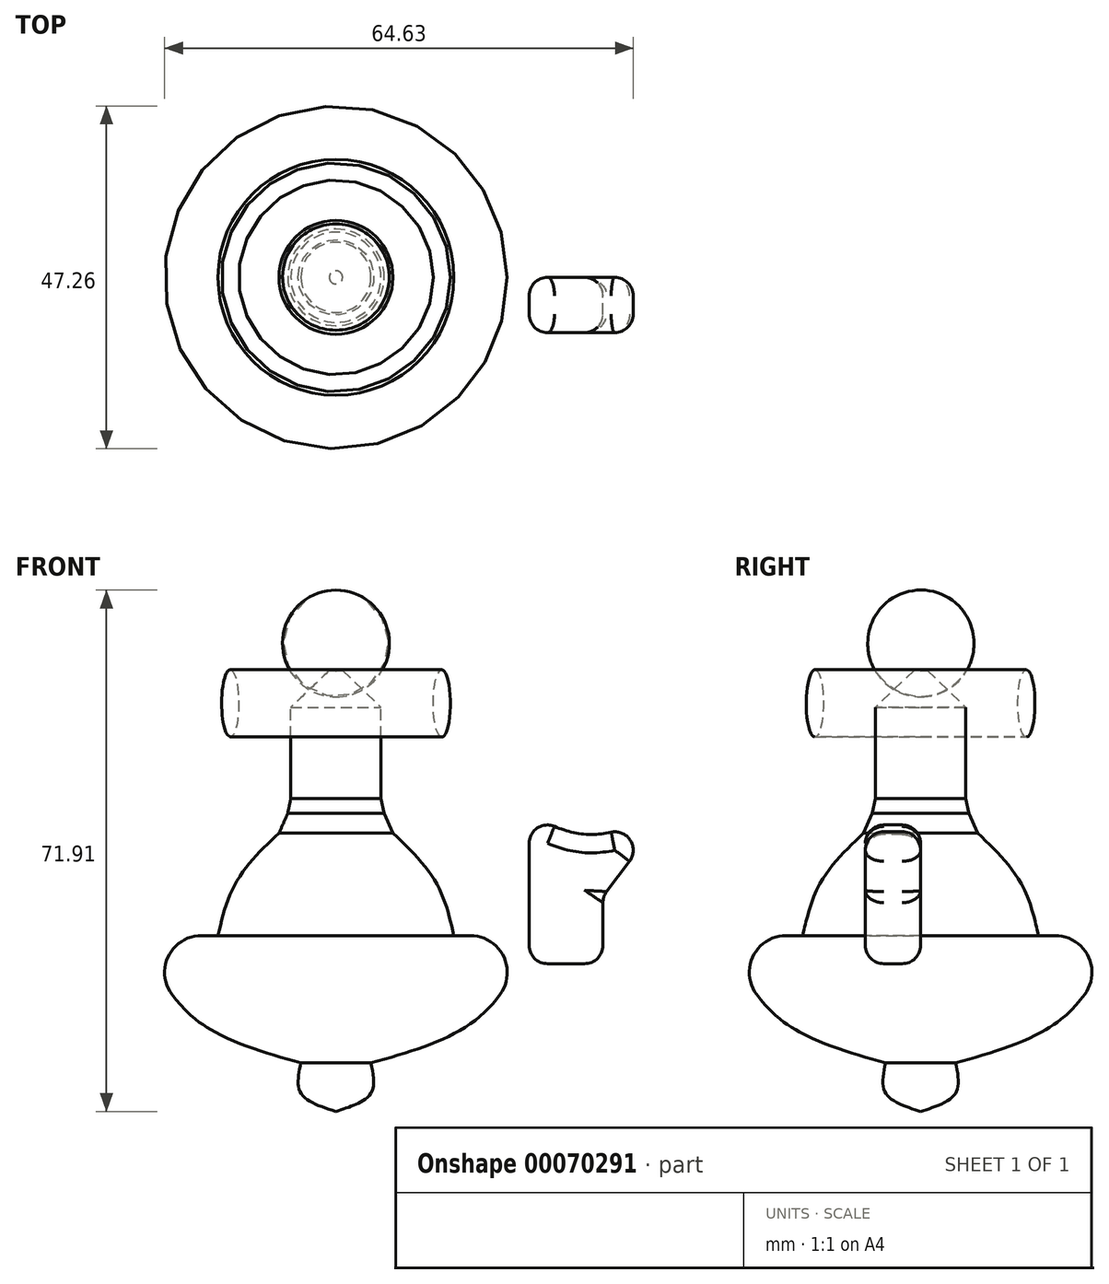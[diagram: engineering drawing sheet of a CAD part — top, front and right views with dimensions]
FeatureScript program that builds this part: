
annotation { "Feature Type Name" : "Feature", "Feature Type Description" : "" }
export const myFeature = defineFeature(function(context is Context, id is Id, definition is map)
    precondition{}
    {
        {
            var Q0;
            Q0=qCreatedBy(makeId("Front.planeOp"),FACE);
            var sketch = newSketch(context, id + "F0", { "sketchPlane" : qUnion([Q0])});
            skLineSegment(sketch, "E0", {"start": v(0, 65.51) * mm, "end": v(0, 4.74) * mm});
            skLineSegment(sketch, "E1", {"start": v(-27.13, 29) * mm, "end": v(-16.26, 29) * mm});
            skLineSegment(sketch, "E2", {"start": v(-6.22, 44.6) * mm, "end": v(-6.22, 65.8) * mm});
            skLineSegment(sketch, "E3", {"start": v(-6.22, 65.8) * mm, "end": v(0, 65.51) * mm});
            skFitSpline(sketch, "E4", {"points": [v(-27.13, 29) * mm, v(-19.63, 17.66) * mm, v(-4.83, 11.43) * mm], "startDerivative": vector(12.61, -26.44) * mm, "endDerivative": vector(31.73, -8.93) * mm});
            skFitSpline(sketch, "E5", {"points": [v(-4.83, 11.43) * mm, v(-4.83, 7.27) * mm, v(0, 4.74) * mm], "startDerivative": vector(-2.1, -9.9) * mm, "endDerivative": vector(11.46, -3.63) * mm});
            skFitSpline(sketch, "E6", {"points": [v(-16.26, 29) * mm, v(-13.62, 36.6) * mm, v(-6.22, 44.6) * mm], "startDerivative": vector(3.85, 16.82) * mm, "endDerivative": vector(15.92, 14.46) * mm});
            skSolve(sketch);
        }
        {
            var Q0;
            Q0=makeQuery(id+"F0.imprint","IMPRINT",FACE,{"disambiguationData":[TD([[makeQuery(id+"F0.imprint","IMPRINT",EDGE,{"derivedFrom":sQuery(id+"F0.wireOp",EDGE,"E0")}),-1.0]])]});
            var Q1;
            Q1=sQuery(id+"F0.wireOp",EDGE,"E0");
            revolve(context, id + "F1", {"entities" : qUnion([Q0]), "axis" : qUnion([Q1]), "revolveType" : RevolveType.FULL});
        }
        {
            var Q0;
            Q0=makeQuery(id+"F1.opRevolve","SWEPT_EDGE",EDGE,{"disambiguationData":[OSD([sQuery(id+"F0.wireOp",EDGE,"E1"),sQuery(id+"F0.wireOp",EDGE,"E4")])]});
            fillet(context, id + "F2", {"entities" : qUnion([Q0]), "radius" : 5.08 * mm, "tangentPropagation" : true, "allowEdgeOverflow" : false});
        }
        {
            var Q0;
            Q0=makeQuery(id+"F1.opRevolve","SWEPT_EDGE",EDGE,{"disambiguationData":[OSD([sQuery(id+"F0.wireOp",EDGE,"E2"),sQuery(id+"F0.wireOp",EDGE,"E6")])]});
            var Q1;
            {var subQ0=sQuery(id+"F0.wireOp",EDGE,"E1");Q1=makeQuery(id+"F2.opFillet","BLEND_EDGE",EDGE,{"blendedFrom":[makeQuery(id+"F1.opRevolve","SWEPT_EDGE",EDGE,{"disambiguationData":[OSD([subQ0,sQuery(id+"F0.wireOp",EDGE,"E4")])]}),makeQuery(id+"F1.opRevolve","SWEPT_FACE",FACE,{"disambiguationData":[OSD([subQ0])]})],"blendedInto":[makeQuery(id+"F1.opRevolve","SWEPT_FACE",FACE,{"disambiguationData":[OSD([subQ0])]})]});}
            chamfer(context, id + "F3", {"entities" : qUnion([Q0, Q1]), "width" : 5.08 * mm, "tangentPropagation" : true});
        }
        {
            var Q0;
            Q0=qCreatedBy(makeId("Right.planeOp"),FACE);
            var sketch = newSketch(context, id + "F4", { "sketchPlane" : qUnion([Q0])});
            skArc(sketch, "E7", {"start": v(-55.27, 0) * mm, "mid": v(-62.6, 7.37) * mm, "end": v(-69.91, 0) * mm});
            skLineSegment(sketch, "E8", {"start": v(-69.91, 0) * mm, "end": v(-55.27, 0) * mm});
            skSolve(sketch);
        }
        {
            var Q0;
            Q0=makeQuery(id+"F4.imprint","IMPRINT",FACE,{"disambiguationData":[TD([[makeQuery(id+"F4.imprint","IMPRINT",EDGE,{"derivedFrom":sQuery(id+"F4.wireOp",EDGE,"E7")}),1.0]])]});
            var Q1;
            Q1=sQuery(id+"F4.wireOp",EDGE,"E8");
            revolve(context, id + "F5", {"entities" : qUnion([Q0]), "axis" : qUnion([Q1]), "revolveType" : RevolveType.FULL});
        }
        {
            var Q0;
            Q0=makeQuery(id+"F5.opRevolve","SWEPT_BODY",BODY,{"disambiguationData":[OSD([sQuery(id+"F4.wireOp",EDGE,"E7"),sQuery(id+"F4.wireOp",EDGE,"E8")])]});
            transform(context, id + "F6", {"entities" : qUnion([Q0]), "transformType" : TransformType.TRANSLATION_3D, "dx" : 0 * mm, "dy" : 62.63 * mm, "dz" : 69.3 * mm, "makeCopy" : false});
        }
        {
            var Q0;
            Q0=qCreatedBy(makeId("Right.planeOp"),FACE);
            var sketch = newSketch(context, id + "F7", { "sketchPlane" : qUnion([Q0])});
            skCircle(sketch, "E9", {"center": v(-15.7, 59.57) * mm, "radius": 3.9 * mm});
            skSolve(sketch);
        }
        {
            var Q0;
            Q0=makeQuery(id+"FKPw20IUTc9UtlZ_2.opSweep","SWEPT_FACE",FACE,{"disambiguationData":[OSD([sQuery(id+"F0.wireOp",EDGE,"E2"),sQuery(id+"F0.wireOp",EDGE,"E6"),sQuery(id+"F7.wireOp",EDGE,"E9")])]});
            var Q1;
            Q1=makeQuery(id+"F1.opRevolve","SWEPT_FACE",FACE,{"disambiguationData":[OSD([sQuery(id+"F0.wireOp",EDGE,"E2")])]});
            chamfer(context, id + "F8", {"entities" : qUnion([Q0, Q1]), "width" : 5.08 * mm, "tangentPropagation" : true});
        }
        {
            var Q0;
            Q0=qCreatedBy(makeId("Front.planeOp"),FACE);
            var sketch = newSketch(context, id + "F9", { "sketchPlane" : qUnion([Q0])});
            skArc(sketch, "E10", {"start": v(-57.67, 0) * mm, "mid": v(-60.56, 2.96) * mm, "end": v(-63.46, 0) * mm});
            skLineSegment(sketch, "E11", {"start": v(-63.46, 0) * mm, "end": v(-57.67, 0) * mm});
            skSolve(sketch);
        }
        {
            var Q0;
            Q0=makeQuery(id+"F9.imprint","IMPRINT",FACE,{"disambiguationData":[TD([[makeQuery(id+"F9.imprint","IMPRINT",EDGE,{"derivedFrom":sQuery(id+"F9.wireOp",EDGE,"E10")}),1.0]])]});
            var Q1;
            Q1=sQuery(id+"F9.wireOp",EDGE,"E11");
            revolve(context, id + "F10", {"entities" : qUnion([Q0]), "axis" : qUnion([Q1]), "revolveType" : RevolveType.FULL});
        }
        {
            var Q0;
            Q0=makeQuery(id+"F10.opRevolve","SWEPT_BODY",BODY,{"disambiguationData":[OSD([sQuery(id+"F9.wireOp",EDGE,"E10"),sQuery(id+"F9.wireOp",EDGE,"E11")])]});
            transform(context, id + "F11", {"entities" : qUnion([Q0]), "transformType" : TransformType.TRANSLATION_3D, "dx" : 60.68 * mm, "dy" : -15.52 * mm, "dz" : 35.43 * mm, "makeCopy" : false});
        }
        {
            var Q0;
            Q0=makeQuery(id+"F10.opRevolve","SWEPT_BODY",BODY,{"disambiguationData":[OSD([sQuery(id+"F9.wireOp",EDGE,"E10"),sQuery(id+"F9.wireOp",EDGE,"E11")])]});
            var Q1;
            Q1=makeQuery(id+"F10.opRevolve","SWEPT_FACE",FACE,{"disambiguationData":[OSD([sQuery(id+"F9.wireOp",EDGE,"E10")])]});
            var Q2;
            {var subQ0=sQuery(id+"F0.wireOp",EDGE,"E1");Q2=makeQuery(id+"F2.opFillet","BLEND_EDGE",EDGE,{"blendedFrom":[makeQuery(id+"F1.opRevolve","SWEPT_EDGE",EDGE,{"disambiguationData":[OSD([subQ0,sQuery(id+"F0.wireOp",EDGE,"E4")])]}),makeQuery(id+"F1.opRevolve","SWEPT_FACE",FACE,{"disambiguationData":[OSD([subQ0])]})],"blendedInto":[makeQuery(id+"F1.opRevolve","SWEPT_FACE",FACE,{"disambiguationData":[OSD([subQ0])]})]});}
            circularPattern(context, id + "F12", {"faces" : qUnion([Q1]), "axis" : qUnion([Q2]), "angle" : 360 * degree, "instanceCount" : 6, "equalSpace" : true, "patternType" : PatternType.FACE});
        }
        {
            var Q0;
            Q0=qCreatedBy(makeId("Front.planeOp"),FACE);
            var sketch = newSketch(context, id + "F13", { "sketchPlane" : qUnion([Q0])});
            skEllipse(sketch, "E12", {"center": v(-14.6, 61.02) * mm, "majorRadius": 4.63 * mm, "minorRadius": 1.18 * mm, "majorAxis": v(0, -1)});
            skSolve(sketch);
        }
        {
            var Q0;
            Q0=makeQuery(id+"F13.imprint","IMPRINT",FACE,{"disambiguationData":[TD([[makeQuery(id+"F13.imprint","IMPRINT",EDGE,{"derivedFrom":sQuery(id+"F13.wireOp",EDGE,"E12")}),1.0]])]});
            var Q1;
            {var subQ0=sQuery(id+"F0.wireOp",EDGE,"E2");var subQ1=makeQuery(id+"F1.opRevolve","SWEPT_FACE",FACE,{"disambiguationData":[OSD([subQ0])]});Q1=makeQuery(id+"F8.opChamfer","BLEND_EDGE",EDGE,{"blendedFrom":[makeQuery(id+"F3.opChamfer","BLEND_EDGE",EDGE,{"blendedFrom":[makeQuery(id+"F1.opRevolve","SWEPT_EDGE",EDGE,{"disambiguationData":[OSD([subQ0,sQuery(id+"F0.wireOp",EDGE,"E6")])]}),subQ1],"blendedInto":[subQ1]}),subQ1],"blendedInto":[subQ1]});}
            sweep(context, id + "F14", {"profiles" : qUnion([Q0]), "path" : qUnion([Q1])});
        }
        {
            var Q0;
            Q0=makeQuery(id+"F10.opRevolve","SWEPT_BODY",BODY,{"disambiguationData":[OSD([sQuery(id+"F9.wireOp",EDGE,"E10"),sQuery(id+"F9.wireOp",EDGE,"E11")])]});
            var Q1;
            Q1=makeQuery(id+"F12.opPattern","COPY",BODY,{"derivedFrom":makeQuery(id+"F10.opRevolve","SWEPT_BODY",BODY,{"disambiguationData":[OSD([sQuery(id+"F9.wireOp",EDGE,"E10"),sQuery(id+"F9.wireOp",EDGE,"E11")])]}),"instanceName":"1"});
            var Q2;
            Q2=makeQuery(id+"F12.opPattern","COPY",BODY,{"derivedFrom":makeQuery(id+"F10.opRevolve","SWEPT_BODY",BODY,{"disambiguationData":[OSD([sQuery(id+"F9.wireOp",EDGE,"E10"),sQuery(id+"F9.wireOp",EDGE,"E11")])]}),"instanceName":"5"});
            var Q3;
            Q3=makeQuery(id+"F12.opPattern","COPY",BODY,{"derivedFrom":makeQuery(id+"F10.opRevolve","SWEPT_BODY",BODY,{"disambiguationData":[OSD([sQuery(id+"F9.wireOp",EDGE,"E10"),sQuery(id+"F9.wireOp",EDGE,"E11")])]}),"instanceName":"2"});
            var Q4;
            Q4=makeQuery(id+"F12.opPattern","COPY",BODY,{"derivedFrom":makeQuery(id+"F10.opRevolve","SWEPT_BODY",BODY,{"disambiguationData":[OSD([sQuery(id+"F9.wireOp",EDGE,"E10"),sQuery(id+"F9.wireOp",EDGE,"E11")])]}),"instanceName":"3"});
            var Q5;
            Q5=makeQuery(id+"F12.opPattern","COPY",BODY,{"derivedFrom":makeQuery(id+"F10.opRevolve","SWEPT_BODY",BODY,{"disambiguationData":[OSD([sQuery(id+"F9.wireOp",EDGE,"E10"),sQuery(id+"F9.wireOp",EDGE,"E11")])]}),"instanceName":"4"});
            var Q6;
            Q6=makeQuery(id+"F5.opRevolve","SWEPT_BODY",BODY,{"disambiguationData":[OSD([sQuery(id+"F4.wireOp",EDGE,"E7"),sQuery(id+"F4.wireOp",EDGE,"E8")])]});
            booleanBodies(context, id + "F15", {"operationType" : BooleanOperationType.SUBTRACTION, "tools" : qUnion([Q0, Q1, Q2, Q3, Q4, Q5]), "targets" : qUnion([Q6])});
        }
        {
            var Q0;
            Q0=qCreatedBy(makeId("Front.planeOp"),FACE);
            var sketch = newSketch(context, id + "F16", { "sketchPlane" : qUnion([Q0])});
            skLineSegment(sketch, "E13", {"start": v(26.63, 45.73) * mm, "end": v(26.63, 25.12) * mm});
            skLineSegment(sketch, "E14", {"start": v(26.63, 25.12) * mm, "end": v(36.82, 25.12) * mm});
            skLineSegment(sketch, "E15", {"start": v(36.82, 25.12) * mm, "end": v(36.82, 34.38) * mm});
            skLineSegment(sketch, "E16", {"start": v(36.82, 34.38) * mm, "end": v(45.4, 45.73) * mm});
            skFitSpline(sketch, "E17", {"points": [v(26.63, 45.73) * mm, v(34.74, 42.95) * mm, v(45.4, 45.73) * mm], "startDerivative": vector(16.65, -8.54) * mm, "endDerivative": vector(20.78, 8.2) * mm});
            skSolve(sketch);
        }
        {
            var Q0;
            Q0=makeQuery(id+"F16.imprint","IMPRINT",FACE,{"disambiguationData":[TD([[makeQuery(id+"F16.imprint","IMPRINT",EDGE,{"derivedFrom":sQuery(id+"F16.wireOp",EDGE,"E13")}),1.0]])]});
            extrude(context, id + "F17", {"entities" : qUnion([Q0]), "depth" : 7.62 * mm});
        }
        {
            var Q0;
            Q0=makeQuery(id+"F17.opExtrude","CAP_EDGE",EDGE,{"disambiguationData":[OSD([sQuery(id+"F16.wireOp",EDGE,"E17")])],"isStart":false});
            var Q1;
            Q1=makeQuery(id+"F17.opExtrude","CAP_EDGE",EDGE,{"disambiguationData":[OSD([sQuery(id+"F16.wireOp",EDGE,"E13")])],"isStart":false});
            var Q2;
            Q2=makeQuery(id+"F17.opExtrude","CAP_FACE",FACE,{"disambiguationData":[OSD([sQuery(id+"F16.wireOp",EDGE,"E13"),sQuery(id+"F16.wireOp",EDGE,"E14"),sQuery(id+"F16.wireOp",EDGE,"E15"),sQuery(id+"F16.wireOp",EDGE,"E16"),sQuery(id+"F16.wireOp",EDGE,"E17")])],"isStart":false});
            var Q3;
            Q3=makeQuery(id+"F17.opExtrude","CAP_EDGE",EDGE,{"disambiguationData":[OSD([sQuery(id+"F16.wireOp",EDGE,"E16")])],"isStart":true});
            var Q4;
            Q4=makeQuery(id+"F17.opExtrude","CAP_EDGE",EDGE,{"disambiguationData":[OSD([sQuery(id+"F16.wireOp",EDGE,"E14")])],"isStart":true});
            var Q5;
            Q5=makeQuery(id+"F17.opExtrude","CAP_EDGE",EDGE,{"disambiguationData":[OSD([sQuery(id+"F16.wireOp",EDGE,"E15")])],"isStart":true});
            var Q6;
            Q6=makeQuery(id+"F17.opExtrude","CAP_EDGE",EDGE,{"disambiguationData":[OSD([sQuery(id+"F16.wireOp",EDGE,"E13")])],"isStart":true});
            var Q7;
            Q7=makeQuery(id+"F17.opExtrude","CAP_EDGE",EDGE,{"disambiguationData":[OSD([sQuery(id+"F16.wireOp",EDGE,"E17")])],"isStart":true});
            fillet(context, id + "F18", {"entities" : qUnion([Q0, Q1, Q2, Q3, Q4, Q5, Q6, Q7]), "radius" : 2.54 * mm, "tangentPropagation" : true, "allowEdgeOverflow" : false});
        }
        {
            var Q0;
            Q0=makeQuery(id+"F17.opExtrude","SWEPT_EDGE",EDGE,{"disambiguationData":[OSD([sQuery(id+"F16.wireOp",EDGE,"E16"),sQuery(id+"F16.wireOp",EDGE,"E17")])]});
            var Q1;
            {var subQ0=sQuery(id+"F16.wireOp",EDGE,"E13");Q1=makeQuery(id+"F18.opFillet","BLEND_EDGE",EDGE,{"blendedFrom":[makeQuery(id+"F17.opExtrude","CAP_EDGE",EDGE,{"disambiguationData":[OSD([subQ0])],"isStart":false}),makeQuery(id+"F17.opExtrude","CAP_FACE",FACE,{"disambiguationData":[OSD([subQ0,sQuery(id+"F16.wireOp",EDGE,"E14"),sQuery(id+"F16.wireOp",EDGE,"E15"),sQuery(id+"F16.wireOp",EDGE,"E16"),sQuery(id+"F16.wireOp",EDGE,"E17")])],"isStart":false})],"blendedInto":[makeQuery(id+"F17.opExtrude","CAP_FACE",FACE,{"disambiguationData":[OSD([subQ0,sQuery(id+"F16.wireOp",EDGE,"E14"),sQuery(id+"F16.wireOp",EDGE,"E15"),sQuery(id+"F16.wireOp",EDGE,"E16"),sQuery(id+"F16.wireOp",EDGE,"E17")])],"isStart":false})]});}
            var Q2;
            {var subQ0=sQuery(id+"F16.wireOp",EDGE,"E17");Q2=makeQuery(id+"F18.opFillet","BLEND_EDGE",EDGE,{"blendedFrom":[makeQuery(id+"F17.opExtrude","CAP_EDGE",EDGE,{"disambiguationData":[OSD([subQ0])],"isStart":false}),makeQuery(id+"F17.opExtrude","CAP_FACE",FACE,{"disambiguationData":[OSD([sQuery(id+"F16.wireOp",EDGE,"E13"),sQuery(id+"F16.wireOp",EDGE,"E14"),sQuery(id+"F16.wireOp",EDGE,"E15"),sQuery(id+"F16.wireOp",EDGE,"E16"),subQ0])],"isStart":false})],"blendedInto":[makeQuery(id+"F17.opExtrude","CAP_FACE",FACE,{"disambiguationData":[OSD([sQuery(id+"F16.wireOp",EDGE,"E13"),sQuery(id+"F16.wireOp",EDGE,"E14"),sQuery(id+"F16.wireOp",EDGE,"E15"),sQuery(id+"F16.wireOp",EDGE,"E16"),subQ0])],"isStart":false})]});}
            var Q3;
            {var subQ0=sQuery(id+"F16.wireOp",EDGE,"E16");Q3=makeQuery(id+"F18.opFillet","BLEND_EDGE",EDGE,{"blendedFrom":[makeQuery(id+"F17.opExtrude","CAP_EDGE",EDGE,{"disambiguationData":[OSD([subQ0])],"isStart":false}),makeQuery(id+"F17.opExtrude","CAP_FACE",FACE,{"disambiguationData":[OSD([sQuery(id+"F16.wireOp",EDGE,"E13"),sQuery(id+"F16.wireOp",EDGE,"E14"),sQuery(id+"F16.wireOp",EDGE,"E15"),subQ0,sQuery(id+"F16.wireOp",EDGE,"E17")])],"isStart":false})],"blendedInto":[makeQuery(id+"F17.opExtrude","CAP_FACE",FACE,{"disambiguationData":[OSD([sQuery(id+"F16.wireOp",EDGE,"E13"),sQuery(id+"F16.wireOp",EDGE,"E14"),sQuery(id+"F16.wireOp",EDGE,"E15"),subQ0,sQuery(id+"F16.wireOp",EDGE,"E17")])],"isStart":false})]});}
            var Q4;
            {var subQ0=sQuery(id+"F16.wireOp",EDGE,"E15");Q4=makeQuery(id+"F18.opFillet","BLEND_EDGE",EDGE,{"blendedFrom":[makeQuery(id+"F17.opExtrude","CAP_EDGE",EDGE,{"disambiguationData":[OSD([subQ0])],"isStart":false}),makeQuery(id+"F17.opExtrude","CAP_FACE",FACE,{"disambiguationData":[OSD([sQuery(id+"F16.wireOp",EDGE,"E13"),sQuery(id+"F16.wireOp",EDGE,"E14"),subQ0,sQuery(id+"F16.wireOp",EDGE,"E16"),sQuery(id+"F16.wireOp",EDGE,"E17")])],"isStart":false})],"blendedInto":[makeQuery(id+"F17.opExtrude","CAP_FACE",FACE,{"disambiguationData":[OSD([sQuery(id+"F16.wireOp",EDGE,"E13"),sQuery(id+"F16.wireOp",EDGE,"E14"),subQ0,sQuery(id+"F16.wireOp",EDGE,"E16"),sQuery(id+"F16.wireOp",EDGE,"E17")])],"isStart":false})]});}
            var Q5;
            {var subQ0=sQuery(id+"F16.wireOp",EDGE,"E14");Q5=makeQuery(id+"F18.opFillet","BLEND_EDGE",EDGE,{"blendedFrom":[makeQuery(id+"F17.opExtrude","CAP_EDGE",EDGE,{"disambiguationData":[OSD([subQ0])],"isStart":false}),makeQuery(id+"F17.opExtrude","CAP_FACE",FACE,{"disambiguationData":[OSD([sQuery(id+"F16.wireOp",EDGE,"E13"),subQ0,sQuery(id+"F16.wireOp",EDGE,"E15"),sQuery(id+"F16.wireOp",EDGE,"E16"),sQuery(id+"F16.wireOp",EDGE,"E17")])],"isStart":false})],"blendedInto":[makeQuery(id+"F17.opExtrude","CAP_FACE",FACE,{"disambiguationData":[OSD([sQuery(id+"F16.wireOp",EDGE,"E13"),subQ0,sQuery(id+"F16.wireOp",EDGE,"E15"),sQuery(id+"F16.wireOp",EDGE,"E16"),sQuery(id+"F16.wireOp",EDGE,"E17")])],"isStart":false})]});}
            var Q6;
            {var subQ0=sQuery(id+"F16.wireOp",EDGE,"E14");Q6=makeQuery(id+"F18.opFillet","BLEND_EDGE",EDGE,{"blendedFrom":[makeQuery(id+"F17.opExtrude","CAP_EDGE",EDGE,{"disambiguationData":[OSD([subQ0])],"isStart":false}),makeQuery(id+"F17.opExtrude","SWEPT_FACE",FACE,{"disambiguationData":[OSD([subQ0])]})],"blendedInto":[makeQuery(id+"F17.opExtrude","SWEPT_FACE",FACE,{"disambiguationData":[OSD([subQ0])]})]});}
            var Q7;
            Q7=makeQuery(id+"F18.opFillet","BLEND_EDGE",EDGE,{"blendedFrom":[makeQuery(id+"F17.opExtrude","CAP_EDGE",EDGE,{"disambiguationData":[OSD([sQuery(id+"F16.wireOp",EDGE,"E13")])],"isStart":false}),makeQuery(id+"F17.opExtrude","CAP_EDGE",EDGE,{"disambiguationData":[OSD([sQuery(id+"F16.wireOp",EDGE,"E14")])],"isStart":false})],"blendedInto":[]});
            var Q8;
            Q8=makeQuery(id+"F18.opFillet","BLEND_EDGE",EDGE,{"blendedFrom":[makeQuery(id+"F17.opExtrude","CAP_EDGE",EDGE,{"disambiguationData":[OSD([sQuery(id+"F16.wireOp",EDGE,"E14")])],"isStart":false}),makeQuery(id+"F17.opExtrude","CAP_EDGE",EDGE,{"disambiguationData":[OSD([sQuery(id+"F16.wireOp",EDGE,"E15")])],"isStart":false})],"blendedInto":[]});
            var Q9;
            Q9=makeQuery(id+"F18.opFillet","BLEND_EDGE",EDGE,{"blendedFrom":[makeQuery(id+"F17.opExtrude","CAP_EDGE",EDGE,{"disambiguationData":[OSD([sQuery(id+"F16.wireOp",EDGE,"E15")])],"isStart":false}),makeQuery(id+"F17.opExtrude","CAP_EDGE",EDGE,{"disambiguationData":[OSD([sQuery(id+"F16.wireOp",EDGE,"E16")])],"isStart":false})],"blendedInto":[]});
            var Q10;
            {var subQ0=sQuery(id+"F16.wireOp",EDGE,"E15");Q10=makeQuery(id+"F18.opFillet","BLEND_EDGE",EDGE,{"blendedFrom":[makeQuery(id+"F17.opExtrude","CAP_EDGE",EDGE,{"disambiguationData":[OSD([subQ0])],"isStart":false}),makeQuery(id+"F17.opExtrude","SWEPT_FACE",FACE,{"disambiguationData":[OSD([subQ0])]})],"blendedInto":[makeQuery(id+"F17.opExtrude","SWEPT_FACE",FACE,{"disambiguationData":[OSD([subQ0])]})]});}
            var Q11;
            {var subQ0=sQuery(id+"F16.wireOp",EDGE,"E13");Q11=makeQuery(id+"F18.opFillet","BLEND_EDGE",EDGE,{"blendedFrom":[makeQuery(id+"F17.opExtrude","CAP_EDGE",EDGE,{"disambiguationData":[OSD([subQ0])],"isStart":false}),makeQuery(id+"F17.opExtrude","SWEPT_FACE",FACE,{"disambiguationData":[OSD([subQ0])]})],"blendedInto":[makeQuery(id+"F17.opExtrude","SWEPT_FACE",FACE,{"disambiguationData":[OSD([subQ0])]})]});}
            var Q12;
            Q12=makeQuery(id+"F18.opFillet","BLEND_EDGE",EDGE,{"blendedFrom":[makeQuery(id+"F17.opExtrude","CAP_EDGE",EDGE,{"disambiguationData":[OSD([sQuery(id+"F16.wireOp",EDGE,"E13")])],"isStart":false}),makeQuery(id+"F17.opExtrude","CAP_EDGE",EDGE,{"disambiguationData":[OSD([sQuery(id+"F16.wireOp",EDGE,"E17")])],"isStart":false})],"blendedInto":[]});
            var Q13;
            {var subQ0=sQuery(id+"F16.wireOp",EDGE,"E16");Q13=makeQuery(id+"F18.opFillet","BLEND_EDGE",EDGE,{"blendedFrom":[makeQuery(id+"F17.opExtrude","CAP_EDGE",EDGE,{"disambiguationData":[OSD([subQ0])],"isStart":false}),makeQuery(id+"F17.opExtrude","SWEPT_FACE",FACE,{"disambiguationData":[OSD([subQ0])]})],"blendedInto":[makeQuery(id+"F17.opExtrude","SWEPT_FACE",FACE,{"disambiguationData":[OSD([subQ0])]})]});}
            var Q14;
            {var subQ0=sQuery(id+"F16.wireOp",EDGE,"E16");Q14=makeQuery(id+"F18.opFillet","BLEND_EDGE",EDGE,{"blendedFrom":[makeQuery(id+"F17.opExtrude","CAP_EDGE",EDGE,{"disambiguationData":[OSD([subQ0])],"isStart":true}),makeQuery(id+"F17.opExtrude","CAP_FACE",FACE,{"disambiguationData":[OSD([sQuery(id+"F16.wireOp",EDGE,"E13"),sQuery(id+"F16.wireOp",EDGE,"E14"),sQuery(id+"F16.wireOp",EDGE,"E15"),subQ0,sQuery(id+"F16.wireOp",EDGE,"E17")])],"isStart":true})],"blendedInto":[makeQuery(id+"F17.opExtrude","CAP_FACE",FACE,{"disambiguationData":[OSD([sQuery(id+"F16.wireOp",EDGE,"E13"),sQuery(id+"F16.wireOp",EDGE,"E14"),sQuery(id+"F16.wireOp",EDGE,"E15"),subQ0,sQuery(id+"F16.wireOp",EDGE,"E17")])],"isStart":true})]});}
            var Q15;
            Q15=makeQuery(id+"F17.opExtrude","SWEPT_EDGE",EDGE,{"disambiguationData":[OSD([sQuery(id+"F16.wireOp",EDGE,"E15"),sQuery(id+"F16.wireOp",EDGE,"E16")])]});
            var Q16;
            Q16=makeQuery(id+"F18.opFillet","BLEND_EDGE",EDGE,{"blendedFrom":[makeQuery(id+"F17.opExtrude","CAP_EDGE",EDGE,{"disambiguationData":[OSD([sQuery(id+"F16.wireOp",EDGE,"E15")])],"isStart":true}),makeQuery(id+"F17.opExtrude","CAP_EDGE",EDGE,{"disambiguationData":[OSD([sQuery(id+"F16.wireOp",EDGE,"E16")])],"isStart":true})],"blendedInto":[]});
            var Q17;
            {var subQ0=sQuery(id+"F16.wireOp",EDGE,"E16");Q17=makeQuery(id+"F18.opFillet","BLEND_EDGE",EDGE,{"blendedFrom":[makeQuery(id+"F17.opExtrude","CAP_EDGE",EDGE,{"disambiguationData":[OSD([subQ0])],"isStart":true}),makeQuery(id+"F17.opExtrude","SWEPT_FACE",FACE,{"disambiguationData":[OSD([subQ0])]})],"blendedInto":[makeQuery(id+"F17.opExtrude","SWEPT_FACE",FACE,{"disambiguationData":[OSD([subQ0])]})]});}
            var Q18;
            {var subQ0=sQuery(id+"F16.wireOp",EDGE,"E15");Q18=makeQuery(id+"F18.opFillet","BLEND_EDGE",EDGE,{"blendedFrom":[makeQuery(id+"F17.opExtrude","CAP_EDGE",EDGE,{"disambiguationData":[OSD([subQ0])],"isStart":true}),makeQuery(id+"F17.opExtrude","SWEPT_FACE",FACE,{"disambiguationData":[OSD([subQ0])]})],"blendedInto":[makeQuery(id+"F17.opExtrude","SWEPT_FACE",FACE,{"disambiguationData":[OSD([subQ0])]})]});}
            var Q19;
            {var subQ0=sQuery(id+"F16.wireOp",EDGE,"E15");Q19=makeQuery(id+"F18.opFillet","BLEND_EDGE",EDGE,{"blendedFrom":[makeQuery(id+"F17.opExtrude","CAP_EDGE",EDGE,{"disambiguationData":[OSD([subQ0])],"isStart":true}),makeQuery(id+"F17.opExtrude","CAP_FACE",FACE,{"disambiguationData":[OSD([sQuery(id+"F16.wireOp",EDGE,"E13"),sQuery(id+"F16.wireOp",EDGE,"E14"),subQ0,sQuery(id+"F16.wireOp",EDGE,"E16"),sQuery(id+"F16.wireOp",EDGE,"E17")])],"isStart":true})],"blendedInto":[makeQuery(id+"F17.opExtrude","CAP_FACE",FACE,{"disambiguationData":[OSD([sQuery(id+"F16.wireOp",EDGE,"E13"),sQuery(id+"F16.wireOp",EDGE,"E14"),subQ0,sQuery(id+"F16.wireOp",EDGE,"E16"),sQuery(id+"F16.wireOp",EDGE,"E17")])],"isStart":true})]});}
            var Q20;
            {var subQ0=sQuery(id+"F16.wireOp",EDGE,"E14");Q20=makeQuery(id+"F18.opFillet","BLEND_EDGE",EDGE,{"blendedFrom":[makeQuery(id+"F17.opExtrude","CAP_EDGE",EDGE,{"disambiguationData":[OSD([subQ0])],"isStart":true}),makeQuery(id+"F17.opExtrude","CAP_FACE",FACE,{"disambiguationData":[OSD([sQuery(id+"F16.wireOp",EDGE,"E13"),subQ0,sQuery(id+"F16.wireOp",EDGE,"E15"),sQuery(id+"F16.wireOp",EDGE,"E16"),sQuery(id+"F16.wireOp",EDGE,"E17")])],"isStart":true})],"blendedInto":[makeQuery(id+"F17.opExtrude","CAP_FACE",FACE,{"disambiguationData":[OSD([sQuery(id+"F16.wireOp",EDGE,"E13"),subQ0,sQuery(id+"F16.wireOp",EDGE,"E15"),sQuery(id+"F16.wireOp",EDGE,"E16"),sQuery(id+"F16.wireOp",EDGE,"E17")])],"isStart":true})]});}
            var Q21;
            {var subQ0=sQuery(id+"F16.wireOp",EDGE,"E13");Q21=makeQuery(id+"F18.opFillet","BLEND_EDGE",EDGE,{"blendedFrom":[makeQuery(id+"F17.opExtrude","CAP_EDGE",EDGE,{"disambiguationData":[OSD([subQ0])],"isStart":true}),makeQuery(id+"F17.opExtrude","CAP_FACE",FACE,{"disambiguationData":[OSD([subQ0,sQuery(id+"F16.wireOp",EDGE,"E14"),sQuery(id+"F16.wireOp",EDGE,"E15"),sQuery(id+"F16.wireOp",EDGE,"E16"),sQuery(id+"F16.wireOp",EDGE,"E17")])],"isStart":true})],"blendedInto":[makeQuery(id+"F17.opExtrude","CAP_FACE",FACE,{"disambiguationData":[OSD([subQ0,sQuery(id+"F16.wireOp",EDGE,"E14"),sQuery(id+"F16.wireOp",EDGE,"E15"),sQuery(id+"F16.wireOp",EDGE,"E16"),sQuery(id+"F16.wireOp",EDGE,"E17")])],"isStart":true})]});}
            var Q22;
            {var subQ0=sQuery(id+"F16.wireOp",EDGE,"E17");Q22=makeQuery(id+"F18.opFillet","BLEND_EDGE",EDGE,{"blendedFrom":[makeQuery(id+"F17.opExtrude","CAP_EDGE",EDGE,{"disambiguationData":[OSD([subQ0])],"isStart":true}),makeQuery(id+"F17.opExtrude","CAP_FACE",FACE,{"disambiguationData":[OSD([sQuery(id+"F16.wireOp",EDGE,"E13"),sQuery(id+"F16.wireOp",EDGE,"E14"),sQuery(id+"F16.wireOp",EDGE,"E15"),sQuery(id+"F16.wireOp",EDGE,"E16"),subQ0])],"isStart":true})],"blendedInto":[makeQuery(id+"F17.opExtrude","CAP_FACE",FACE,{"disambiguationData":[OSD([sQuery(id+"F16.wireOp",EDGE,"E13"),sQuery(id+"F16.wireOp",EDGE,"E14"),sQuery(id+"F16.wireOp",EDGE,"E15"),sQuery(id+"F16.wireOp",EDGE,"E16"),subQ0])],"isStart":true})]});}
            fillet(context, id + "F19", {"entities" : qUnion([Q0, Q1, Q2, Q3, Q4, Q5, Q6, Q7, Q8, Q9, Q10, Q11, Q12, Q13, Q14, Q15, Q16, Q17, Q18, Q19, Q20, Q21, Q22]), "radius" : 2.54 * mm, "tangentPropagation" : true, "allowEdgeOverflow" : false});
        }
        {
            var Q0;
            Q0=qCreatedBy(makeId("Front.planeOp"),FACE);
            var sketch = newSketch(context, id + "F20", { "sketchPlane" : qUnion([Q0])});
            skCircle(sketch, "E18", {"center": v(-51.28, 58.8) * mm, "radius": 10.35 * mm});
            skSolve(sketch);
        }
        {
            var Q0;
            Q0=makeQuery(id+"F20.imprint","IMPRINT",FACE,{"disambiguationData":[TD([[makeQuery(id+"F20.imprint","IMPRINT",EDGE,{"derivedFrom":sQuery(id+"F20.wireOp",EDGE,"E18")}),1.0]])]});
            extrude(context, id + "F21", {"entities" : qUnion([Q0]), "depth" : 2.54 * mm});
        }
        {
            var Q0;
            Q0=qCreatedBy(makeId("Front.planeOp"),FACE);
            var sketch = newSketch(context, id + "F22", { "sketchPlane" : qUnion([Q0])});
            skCircle(sketch, "E19", {"center": v(-46.34, 38) * mm, "radius": 10.14 * mm});
            skSolve(sketch);
        }
        {
            var Q0;
            Q0=makeQuery(id+"F22.imprint","IMPRINT",FACE,{"disambiguationData":[TD([[makeQuery(id+"F22.imprint","IMPRINT",EDGE,{"derivedFrom":sQuery(id+"F22.wireOp",EDGE,"E19")}),1.0]])]});
            extrude(context, id + "F23", {"entities" : qUnion([Q0]), "depth" : 25.4 * mm});
        }
        {
            var Q0;
            Q0=makeQuery(id+"F23.opExtrude","SWEPT_BODY",BODY,{"disambiguationData":[OSD([sQuery(id+"F22.wireOp",EDGE,"E19")])]});
            deleteBodies(context, id + "F24", {"entities" : qUnion([Q0])});
        }
        {
            var Q0;
            Q0=qCreatedBy(makeId("Front.planeOp"),FACE);
            var sketch = newSketch(context, id + "F25", { "sketchPlane" : qUnion([Q0])});
            skCircle(sketch, "E20", {"center": v(-51.54, 36.7) * mm, "radius": 9.11 * mm});
            skSolve(sketch);
        }
        {
            var Q0;
            Q0=makeQuery(id+"F25.imprint","IMPRINT",FACE,{"disambiguationData":[TD([[makeQuery(id+"F25.imprint","IMPRINT",EDGE,{"derivedFrom":sQuery(id+"F25.wireOp",EDGE,"E20")}),1.0]])]});
            extrude(context, id + "F26", {"entities" : qUnion([Q0]), "depth" : 25.4 * mm});
        }
        {
            var Q0;
            Q0=makeQuery(id+"F26.opExtrude","SWEPT_BODY",BODY,{"disambiguationData":[OSD([sQuery(id+"F25.wireOp",EDGE,"E20")])]});
            transform(context, id + "F27", {"entities" : qUnion([Q0]), "transformType" : TransformType.TRANSLATION_3D, "dx" : 0.26 * mm, "dy" : -5.98 * mm, "dz" : 22.1 * mm, "makeCopy" : false});
        }
        {
            var Q0;
            Q0=makeQuery(id+"F26.opExtrude","CAP_FACE",FACE,{"disambiguationData":[OSD([sQuery(id+"F25.wireOp",EDGE,"E20")])],"isStart":false});
            extrude(context, id + "F28", {"entities" : qUnion([Q0]), "operationType" : NewBodyOperationType.REMOVE, "oppositeDirection" : true, "depth" : 62.57 * mm});
        }
        {
            var Q0;
            Q0=makeQuery(id+"F21.opExtrude","SWEPT_BODY",BODY,{"disambiguationData":[OSD([sQuery(id+"F20.wireOp",EDGE,"E18")])]});
            transform(context, id + "F29", {"entities" : qUnion([Q0]), "transformType" : TransformType.TRANSLATION_3D, "dx" : 40.03 * mm, "dy" : -5.46 * mm, "dz" : 3.38 * mm, "makeCopy" : false});
        }
        {
            var Q0;
            Q0=makeQuery(id+"F21.opExtrude","SWEPT_BODY",BODY,{"disambiguationData":[OSD([sQuery(id+"F20.wireOp",EDGE,"E18")])]});
            deleteBodies(context, id + "F30", {"entities" : qUnion([Q0])});
        }
    });
